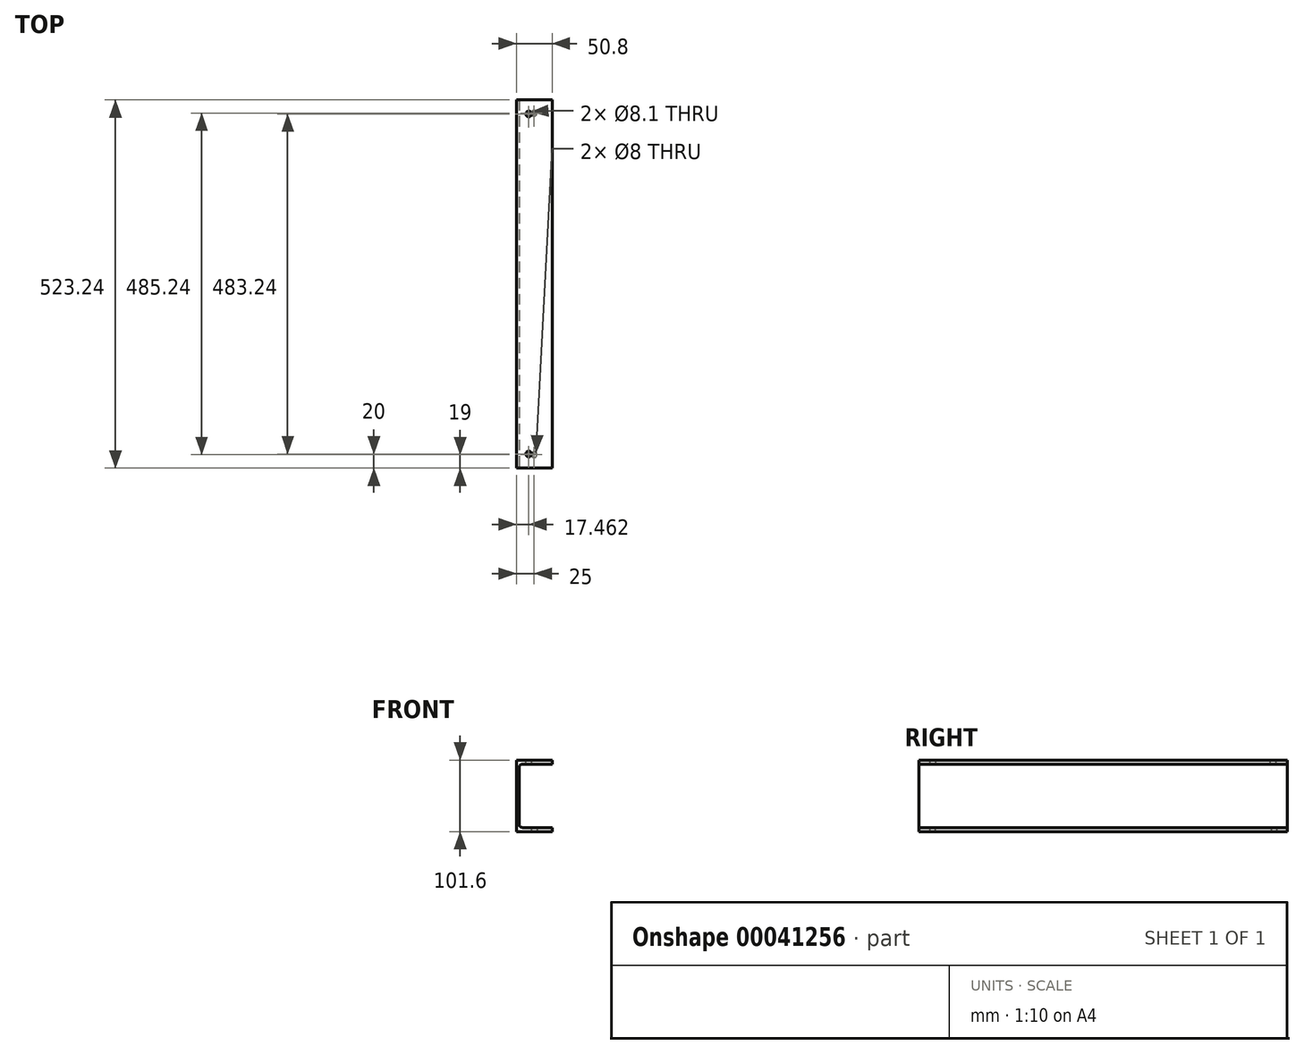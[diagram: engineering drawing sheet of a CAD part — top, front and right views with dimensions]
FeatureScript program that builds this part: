
annotation { "Feature Type Name" : "Feature", "Feature Type Description" : "" }
export const myFeature = defineFeature(function(context is Context, id is Id, definition is map)
    precondition{}
    {
        {
            var Q0;
            Q0=qCreatedBy(makeId("Front.planeOp"),FACE);
            var sketch = newSketch(context, id + "F0", { "sketchPlane" : qUnion([Q0])});
            skLineSegment(sketch, "E0.bottom", {"start": v(0, 0) * mm, "end": v(50.8, 0) * mm});
            skLineSegment(sketch, "E0.top", {"start": v(0, 101.6) * mm, "end": v(50.8, 101.6) * mm});
            skLineSegment(sketch, "E0.left", {"start": v(0, 0) * mm, "end": v(0, 101.6) * mm});
            skLineSegment(sketch, "E0.right", {"start": v(50.8, 0) * mm, "end": v(50.8, 5.84) * mm});
            skLineSegment(sketch, "E1.bottom", {"start": v(3.81, 5.84) * mm, "end": v(50.8, 5.84) * mm});
            skLineSegment(sketch, "E1.top", {"start": v(3.8, 95.76) * mm, "end": v(50.8, 95.76) * mm});
            skLineSegment(sketch, "E1.left", {"start": v(3.8, 5.84) * mm, "end": v(3.8, 95.76) * mm});
            skLineSegment(sketch, "E2.trimOffspring", {"start": v(50.8, 95.76) * mm, "end": v(50.8, 101.6) * mm});
            skSolve(sketch);
        }
        {
            var Q0;
            Q0=makeQuery(id+"F0.imprint","IMPRINT",FACE,{"disambiguationData":[TD([[makeQuery(id+"F0.imprint","IMPRINT",EDGE,{"derivedFrom":sQuery(id+"F0.wireOp",EDGE,"E0.bottom")}),1.0]])]});
            extrude(context, id + "F1", {"entities" : qUnion([Q0]), "oppositeDirection" : true, "depth" : 523.24 * mm});
        }
        {
            var Q0;
            Q0=makeQuery(id+"F1.opExtrude","SWEPT_EDGE",EDGE,{"disambiguationData":[OSD([sQuery(id+"F0.wireOp",EDGE,"E1.bottom"),sQuery(id+"F0.wireOp",EDGE,"E1.left")])]});
            var Q1;
            Q1=makeQuery(id+"F1.opExtrude","SWEPT_EDGE",EDGE,{"disambiguationData":[OSD([sQuery(id+"F0.wireOp",EDGE,"E1.top"),sQuery(id+"F0.wireOp",EDGE,"E1.left")])]});
            fillet(context, id + "F2", {"entities" : qUnion([Q0, Q1]), "radius" : 4.57 * mm, "tangentPropagation" : true, "allowEdgeOverflow" : false});
        }
        {
            var Q0;
            Q0=makeQuery(id+"F1.opExtrude","SWEPT_FACE",FACE,{"disambiguationData":[OSD([sQuery(id+"F0.wireOp",EDGE,"E0.top")])]});
            var sketch = newSketch(context, id + "F3", { "sketchPlane" : qUnion([Q0])});
            skPoint(sketch, "E3", {"position": v(17.46, 503.24) * mm});
            skPoint(sketch, "E4", {"position": v(17.46, 20) * mm});
            skLineSegment(sketch, "E5", {"start": v(0, 261.62) * mm, "end": v(80.89, 261.62) * mm, "construction": true});
            skSolve(sketch);
        }
        {
            var Q0;
            Q0=sQuery(id+"F3.wireOp",VERTEX,"E3");
            var Q1;
            Q1=sQuery(id+"F3.wireOp",VERTEX,"E4");
            var Q2;
            Q2=makeQuery(id+"F1.opExtrude","SWEPT_BODY",BODY,{"disambiguationData":[OSD([sQuery(id+"F0.wireOp",EDGE,"E0.bottom"),sQuery(id+"F0.wireOp",EDGE,"E0.top"),sQuery(id+"F0.wireOp",EDGE,"E0.left"),sQuery(id+"F0.wireOp",EDGE,"E0.right"),sQuery(id+"F0.wireOp",EDGE,"E1.bottom"),sQuery(id+"F0.wireOp",EDGE,"E1.top"),sQuery(id+"F0.wireOp",EDGE,"E1.left"),sQuery(id+"F0.wireOp",EDGE,"E2.trimOffspring")])]});
            hole(context, id + "F4", {"style" : HoleStyle.SIMPLE, "holeDiameter" : 8.1 * mm, "endStyle" : HoleEndStyle.BLIND, "holeDepth" : 20 * mm, "locations" : qUnion([Q0, Q1]), "scope" : qUnion([Q2])});
        }
        {
            var Q0;
            Q0=makeQuery(id+"F1.opExtrude","SWEPT_FACE",FACE,{"disambiguationData":[OSD([sQuery(id+"F0.wireOp",EDGE,"E0.bottom")])]});
            var sketch = newSketch(context, id + "F5", { "sketchPlane" : qUnion([Q0])});
            skPoint(sketch, "E6", {"position": v(25, -19) * mm});
            skPoint(sketch, "E7", {"position": v(25, -504.24) * mm});
            skSolve(sketch);
        }
        {
            var Q0;
            Q0=sQuery(id+"F5.wireOp",VERTEX,"E6");
            var Q1;
            Q1=sQuery(id+"F5.wireOp",VERTEX,"E7");
            var Q2;
            Q2=makeQuery(id+"F1.opExtrude","SWEPT_BODY",BODY,{"disambiguationData":[OSD([sQuery(id+"F0.wireOp",EDGE,"E0.bottom"),sQuery(id+"F0.wireOp",EDGE,"E0.top"),sQuery(id+"F0.wireOp",EDGE,"E0.left"),sQuery(id+"F0.wireOp",EDGE,"E0.right"),sQuery(id+"F0.wireOp",EDGE,"E1.bottom"),sQuery(id+"F0.wireOp",EDGE,"E1.top"),sQuery(id+"F0.wireOp",EDGE,"E1.left"),sQuery(id+"F0.wireOp",EDGE,"E2.trimOffspring")])]});
            hole(context, id + "F6", {"style" : HoleStyle.SIMPLE, "holeDiameter" : 8 * mm, "endStyle" : HoleEndStyle.BLIND, "holeDepth" : 10 * mm, "locations" : qUnion([Q0, Q1]), "scope" : qUnion([Q2])});
        }
    });
